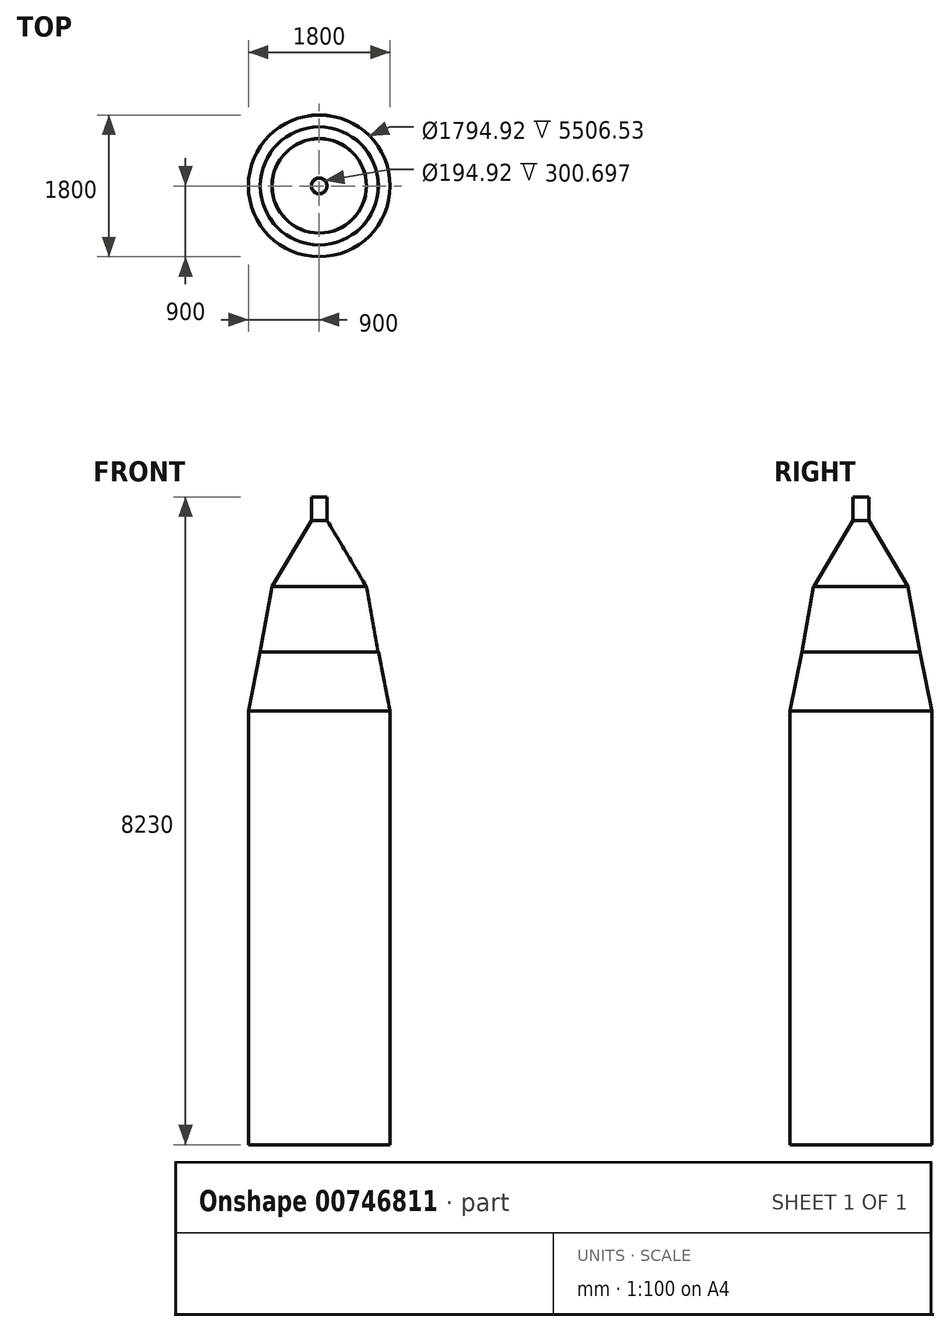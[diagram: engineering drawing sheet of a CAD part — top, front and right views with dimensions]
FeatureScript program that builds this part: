
annotation { "Feature Type Name" : "Feature", "Feature Type Description" : "" }
export const myFeature = defineFeature(function(context is Context, id is Id, definition is map)
    precondition{}
    {
        {
            var Q0;
            Q0=qCreatedBy(makeId("Top.planeOp"),FACE);
            var sketch = newSketch(context, id + "F0", { "sketchPlane" : qUnion([Q0])});
            skCircle(sketch, "E0", {"center": v(0, 0) * mm, "radius": 900 * mm});
            skSolve(sketch);
        }
        {
            var Q0;
            Q0=qSketchRegion(id+"F0",true);
            extrude(context, id + "F1", {"entities" : qUnion([Q0]), "depth" : 5510 * mm, "offsetDistance" : 25.4 * mm});
        }
        {
            var Q0;
            Q0=makeQuery(id+"F1.opExtrude","CAP_FACE",FACE,{"disambiguationData":[OSD([sQuery(id+"F0.wireOp",EDGE,"E0")])],"isStart":false});
            cPlane(context, id + "F2", {"entities" : qUnion([Q0]), "cplaneType" : CPlaneType.OFFSET, "offset" : 750 * mm, "width" : 152.4 * mm, "height" : 152.4 * mm});
        }
        {
            var Q0;
            Q0=qCreatedBy(id+"F2.planeOp",FACE);
            var sketch = newSketch(context, id + "F3", { "sketchPlane" : qUnion([Q0])});
            skCircle(sketch, "E1", {"center": v(0, 0) * mm, "radius": 750 * mm});
            skSolve(sketch);
        }
        {
            var Q0;
            Q0=makeQuery(id+"F3.imprint","IMPRINT",FACE,{"disambiguationData":[TD([[makeQuery(id+"F3.imprint","IMPRINT",EDGE,{"derivedFrom":sQuery(id+"F3.wireOp",EDGE,"E1")}),1.0]])]});
            var Q1;
            Q1=makeQuery(id+"F1.opExtrude","CAP_FACE",FACE,{"disambiguationData":[OSD([sQuery(id+"F0.wireOp",EDGE,"E0")])],"isStart":false});
            extrude(context, id + "F4", {"entities" : qUnion([Q0]), "operationType" : NewBodyOperationType.ADD, "endBound" : BoundingType.UP_TO_SURFACE, "oppositeDirection" : true, "depth" : 25.4 * mm, "endBoundEntityFace" : qUnion([Q1]), "offsetDistance" : 25.4 * mm, "hasDraft" : true, "draftAngle" : 11.3 * degree});
        }
        {
            var Q0;
            Q0=makeQuery(id+"F4.opExtrude","CAP_FACE",FACE,{"disambiguationData":[OSD([sQuery(id+"F3.wireOp",EDGE,"E1")])],"isStart":true});
            cPlane(context, id + "F5", {"entities" : qUnion([Q0]), "cplaneType" : CPlaneType.OFFSET, "offset" : 830 * mm, "width" : 152.4 * mm, "height" : 152.4 * mm});
        }
        {
            var Q0;
            Q0=qCreatedBy(id+"F5.planeOp",FACE);
            var sketch = newSketch(context, id + "F6", { "sketchPlane" : qUnion([Q0])});
            skCircle(sketch, "E2", {"center": v(0, 0) * mm, "radius": 600 * mm});
            skSolve(sketch);
        }
        {
            var Q0;
            Q0=qSketchRegion(id+"F6",true);
            var Q1;
            Q1=makeQuery(id+"F4.opExtrude","CAP_FACE",FACE,{"disambiguationData":[OSD([sQuery(id+"F3.wireOp",EDGE,"E1")])],"isStart":true});
            extrude(context, id + "F7", {"entities" : qUnion([Q0]), "operationType" : NewBodyOperationType.ADD, "endBound" : BoundingType.UP_TO_SURFACE, "oppositeDirection" : true, "depth" : 25.4 * mm, "endBoundEntityFace" : qUnion([Q1]), "offsetDistance" : 25.4 * mm, "hasDraft" : true, "draftAngle" : 10.2 * degree});
        }
        {
            var Q0;
            Q0=makeQuery(id+"F7.opExtrude","CAP_FACE",FACE,{"disambiguationData":[OSD([sQuery(id+"F6.wireOp",EDGE,"E2")])],"isStart":true});
            cPlane(context, id + "F8", {"entities" : qUnion([Q0]), "cplaneType" : CPlaneType.OFFSET, "offset" : 840 * mm, "width" : 152.4 * mm, "height" : 152.4 * mm});
        }
        {
            var Q0;
            Q0=qCreatedBy(id+"F8.planeOp",FACE);
            var sketch = newSketch(context, id + "F9", { "sketchPlane" : qUnion([Q0])});
            skCircle(sketch, "E3", {"center": v(0, 0) * mm, "radius": 100 * mm});
            skSolve(sketch);
        }
        {
            var Q0;
            Q0=qSketchRegion(id+"F9",true);
            var Q1;
            Q1=makeQuery(id+"F7.opExtrude","CAP_FACE",FACE,{"disambiguationData":[OSD([sQuery(id+"F6.wireOp",EDGE,"E2")])],"isStart":true});
            extrude(context, id + "F10", {"entities" : qUnion([Q0]), "operationType" : NewBodyOperationType.ADD, "endBound" : BoundingType.UP_TO_SURFACE, "oppositeDirection" : true, "depth" : 25.4 * mm, "endBoundEntityFace" : qUnion([Q1]), "offsetDistance" : 25.4 * mm, "hasDraft" : true, "draftAngle" : 30.7 * degree});
        }
        {
            var Q0;
            Q0=makeQuery(id+"F10.opExtrude","CAP_FACE",FACE,{"disambiguationData":[OSD([sQuery(id+"F9.wireOp",EDGE,"E3")])],"isStart":true});
            var sketch = newSketch(context, id + "F11", { "sketchPlane" : qUnion([Q0])});
            skCircle(sketch, "E4", {"center": v(0, 0) * mm, "radius": 100 * mm});
            skSolve(sketch);
        }
        {
            var Q0;
            Q0=qSketchRegion(id+"F11",true);
            extrude(context, id + "F12", {"entities" : qUnion([Q0]), "operationType" : NewBodyOperationType.ADD, "depth" : 300 * mm, "offsetDistance" : 25.4 * mm});
        }
        {
            var Q0;
            Q0=makeQuery(id+"F12.opExtrude","CAP_FACE",FACE,{"disambiguationData":[OSD([sQuery(id+"F11.wireOp",EDGE,"E4")])],"isStart":false});
            shell(context, id + "F13", {"entities" : qUnion([Q0]), "thickness" : 2.54 * mm});
        }
    });
